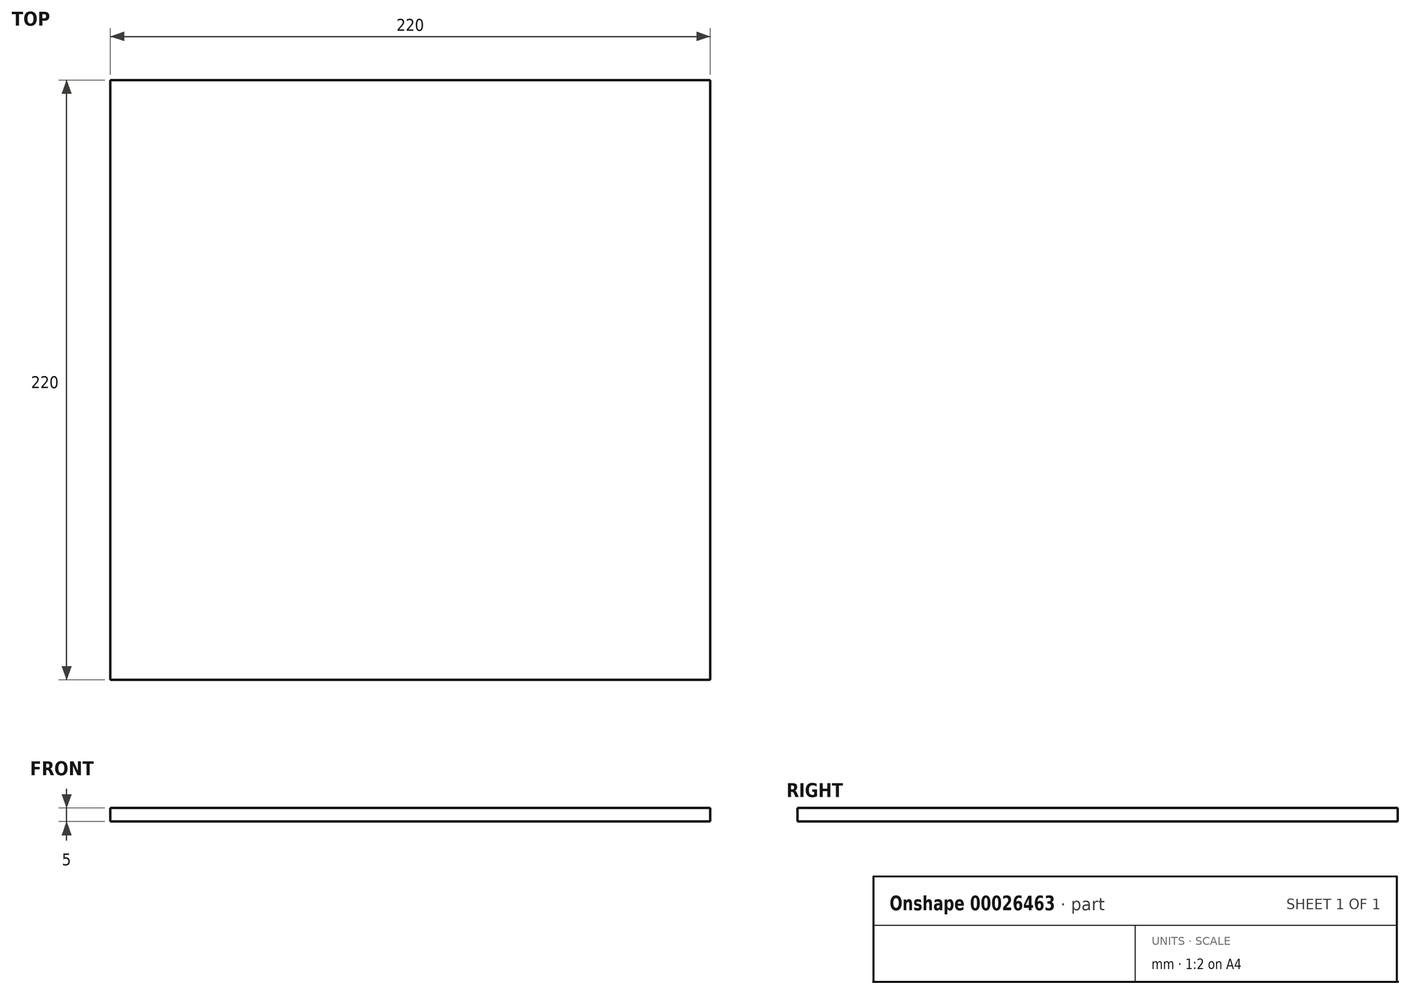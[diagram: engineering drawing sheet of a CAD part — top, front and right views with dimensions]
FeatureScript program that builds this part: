
annotation { "Feature Type Name" : "Feature", "Feature Type Description" : "" }
export const myFeature = defineFeature(function(context is Context, id is Id, definition is map)
    precondition{}
    {
        {
            var Q0;
            Q0=qCreatedBy(makeId("Top.planeOp"),FACE);
            var sketch = newSketch(context, id + "F0", { "sketchPlane" : qUnion([Q0])});
            skLineSegment(sketch, "E0.rect.bottom", {"start": v(-110, 110) * mm, "end": v(110, 110) * mm});
            skLineSegment(sketch, "E0.rect.top", {"start": v(-110, -110) * mm, "end": v(110, -110) * mm});
            skLineSegment(sketch, "E0.rect.left", {"start": v(-110, 110) * mm, "end": v(-110, -110) * mm});
            skLineSegment(sketch, "E0.rect.right", {"start": v(110, 110) * mm, "end": v(110, -110) * mm});
            skPoint(sketch, "E0.rect.middle", {"position": v(0, 0) * mm});
            skSolve(sketch);
        }
        {
            var Q0;
            Q0 = qSketchRegion(id + "F0", true);
            extrude(context, id + "F1", {"entities" : qUnion([Q0]), "depth" : 5 * mm});
        }
        {
            var Q0;
            Q0=makeQuery(id+"F1.opExtrude","CAP_FACE",FACE,{"disambiguationData":[OSD([sQuery(id+"F0.wireOp",EDGE,"E0.rect.bottom"),sQuery(id+"F0.wireOp",EDGE,"E0.rect.top"),sQuery(id+"F0.wireOp",EDGE,"E0.rect.left"),sQuery(id+"F0.wireOp",EDGE,"E0.rect.right")])],"isStart":true});
            var sketch = newSketch(context, id + "F2", { "sketchPlane" : qUnion([Q0])});
            skLineSegment(sketch, "E1", {"start": v(-80, 0) * mm, "end": v(80, 0) * mm});
            skPoint(sketch, "E1.endSnap0", {"position": v(110, 0) * mm});
            skPoint(sketch, "E2", {"position": v(0, 0) * mm});
            skSolve(sketch);
        }
    });
